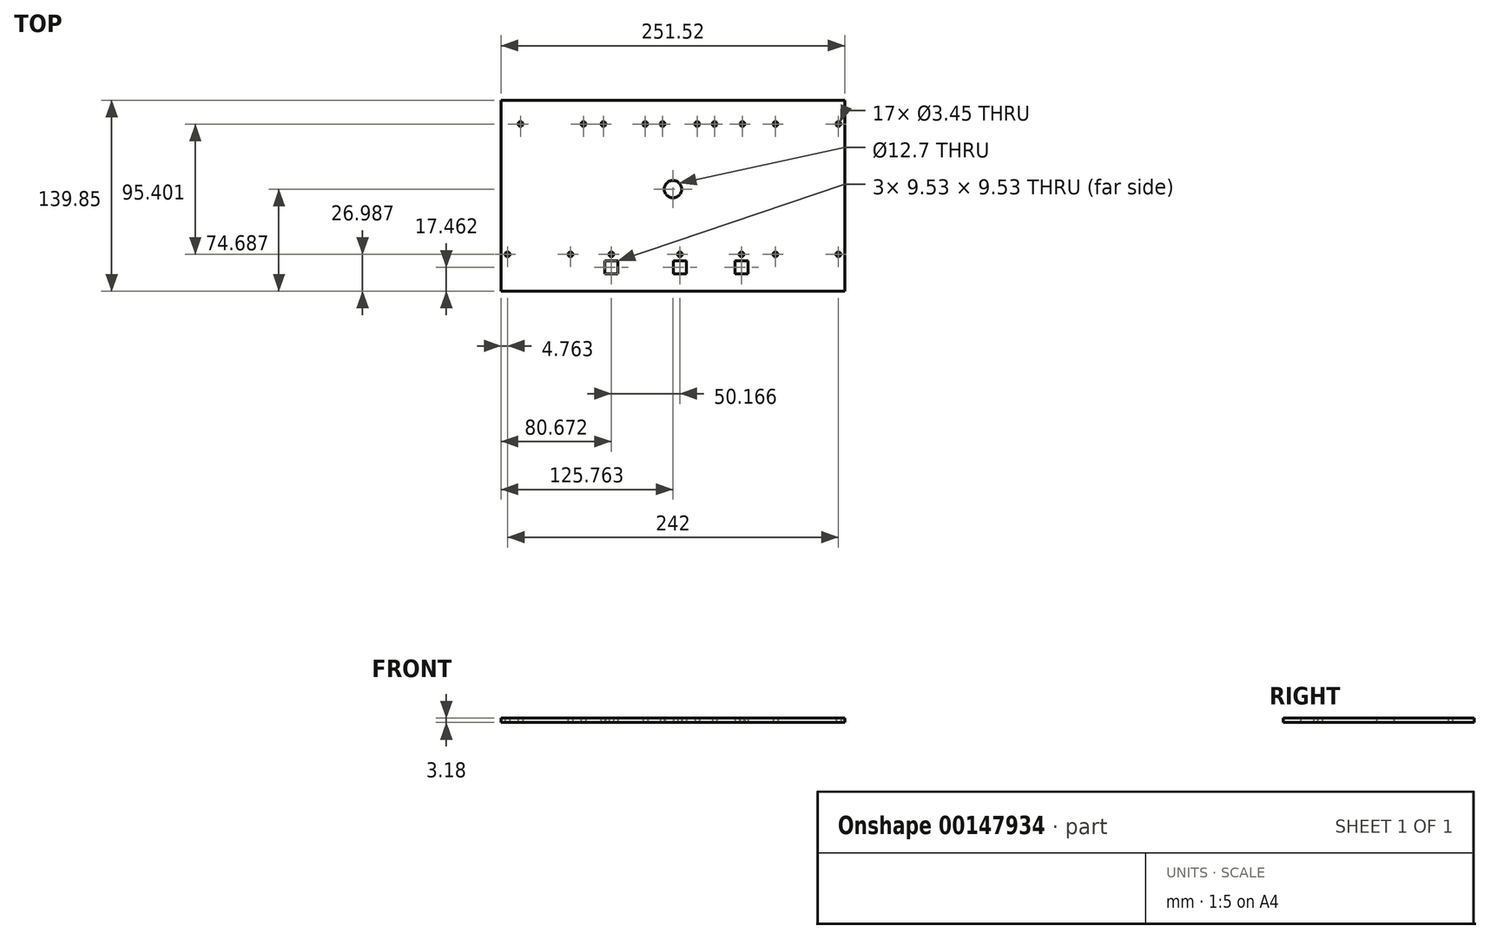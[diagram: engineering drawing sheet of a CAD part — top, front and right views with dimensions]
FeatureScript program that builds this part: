
annotation { "Feature Type Name" : "Feature", "Feature Type Description" : "" }
export const myFeature = defineFeature(function(context is Context, id is Id, definition is map)
    precondition{}
    {
        {
            var Q0;
            Q0=qCreatedBy(makeId("Top.planeOp"),FACE);
            var sketch = newSketch(context, id + "F0", { "sketchPlane" : qUnion([Q0])});
            skLineSegment(sketch, "E0.bottom", {"start": v(0, 0) * mm, "end": v(251.52, 0) * mm});
            skLineSegment(sketch, "E0.top", {"start": v(0, -139.85) * mm, "end": v(251.52, -139.85) * mm});
            skLineSegment(sketch, "E0.left", {"start": v(0, 0) * mm, "end": v(0, -139.85) * mm});
            skLineSegment(sketch, "E0.right", {"start": v(251.52, 0) * mm, "end": v(251.52, -139.85) * mm});
            skLineSegment(sketch, "E1", {"start": v(14.29, 0) * mm, "end": v(14.29, -17.46) * mm, "construction": true});
            skLineSegment(sketch, "E2", {"start": v(14.29, -17.46) * mm, "end": v(0, -17.46) * mm, "construction": true});
            skLineSegment(sketch, "E3", {"start": v(14.29, -17.46) * mm, "end": v(60.33, -17.46) * mm, "construction": true});
            skCircle(sketch, "E4", {"center": v(14.29, -17.46) * mm, "radius": 1.73 * mm});
            skCircle(sketch, "E5", {"center": v(60.33, -17.46) * mm, "radius": 1.73 * mm});
            skLineSegment(sketch, "E6", {"start": v(251.52, -17.46) * mm, "end": v(246.76, -17.46) * mm, "construction": true});
            skLineSegment(sketch, "E7", {"start": v(246.76, -17.46) * mm, "end": v(200.72, -17.46) * mm, "construction": true});
            skLineSegment(sketch, "E8", {"start": v(200.72, -17.46) * mm, "end": v(176.6, -17.46) * mm, "construction": true});
            skCircle(sketch, "E9", {"center": v(105.46, -17.46) * mm, "radius": 1.73 * mm});
            skCircle(sketch, "E10", {"center": v(176.6, -17.46) * mm, "radius": 1.73 * mm});
            skCircle(sketch, "E11", {"center": v(200.72, -17.46) * mm, "radius": 1.73 * mm});
            skCircle(sketch, "E12", {"center": v(246.76, -17.46) * mm, "radius": 1.73 * mm});
            skLineSegment(sketch, "E13", {"start": v(4.76, -139.85) * mm, "end": v(4.76, -112.86) * mm, "construction": true});
            skLineSegment(sketch, "E14", {"start": v(4.76, -112.86) * mm, "end": v(50.8, -112.86) * mm, "construction": true});
            skLineSegment(sketch, "E15", {"start": v(186.12, -112.86) * mm, "end": v(200.72, -112.86) * mm, "construction": true});
            skLineSegment(sketch, "E16", {"start": v(200.72, -112.86) * mm, "end": v(246.76, -112.86) * mm, "construction": true});
            skLineSegment(sketch, "E17", {"start": v(246.76, -112.86) * mm, "end": v(251.52, -112.86) * mm, "construction": true});
            skCircle(sketch, "E18", {"center": v(4.76, -112.86) * mm, "radius": 1.73 * mm});
            skCircle(sketch, "E19", {"center": v(50.8, -112.86) * mm, "radius": 1.73 * mm});
            skCircle(sketch, "E20", {"center": v(200.72, -112.86) * mm, "radius": 1.73 * mm});
            skCircle(sketch, "E21", {"center": v(246.76, -112.86) * mm, "radius": 1.73 * mm});
            skLineSegment(sketch, "E22", {"start": v(50.8, -112.86) * mm, "end": v(65.4, -112.86) * mm, "construction": true});
            skLineSegment(sketch, "E23", {"start": v(65.4, -112.86) * mm, "end": v(95.94, -112.86) * mm, "construction": true});
            skLineSegment(sketch, "E24", {"start": v(60.33, -17.46) * mm, "end": v(74.93, -17.46) * mm, "construction": true});
            skCircle(sketch, "E25", {"center": v(74.93, -17.46) * mm, "radius": 1.73 * mm});
            skLineSegment(sketch, "E26", {"start": v(74.93, -17.46) * mm, "end": v(105.46, -17.46) * mm, "construction": true});
            skLineSegment(sketch, "E27", {"start": v(186.12, -112.86) * mm, "end": v(165.74, -112.86) * mm, "construction": true});
            skLineSegment(sketch, "E28", {"start": v(176.6, -17.46) * mm, "end": v(156.21, -17.46) * mm, "construction": true});
            skCircle(sketch, "E29", {"center": v(156.21, -17.46) * mm, "radius": 1.73 * mm});
            skLineSegment(sketch, "E30", {"start": v(165.74, -112.86) * mm, "end": v(153.04, -112.86) * mm, "construction": true});
            skLineSegment(sketch, "E31", {"start": v(95.94, -112.86) * mm, "end": v(108.64, -112.86) * mm, "construction": true});
            skLineSegment(sketch, "E32", {"start": v(156.21, -17.46) * mm, "end": v(143.51, -17.46) * mm, "construction": true});
            skLineSegment(sketch, "E33", {"start": v(105.46, -17.46) * mm, "end": v(118.16, -17.46) * mm, "construction": true});
            skCircle(sketch, "E34", {"center": v(143.51, -17.46) * mm, "radius": 1.73 * mm});
            skCircle(sketch, "E35", {"center": v(118.16, -17.46) * mm, "radius": 1.73 * mm});
            skLineSegment(sketch, "E36", {"start": v(108.64, -112.86) * mm, "end": v(108.64, -65.16) * mm, "construction": true});
            skLineSegment(sketch, "E37", {"start": v(108.64, -65.16) * mm, "end": v(125.76, -65.16) * mm, "construction": true});
            skLineSegment(sketch, "E38", {"start": v(118.16, -17.46) * mm, "end": v(125.76, -17.46) * mm, "construction": true});
            skLineSegment(sketch, "E39", {"start": v(125.76, -65.16) * mm, "end": v(125.76, -17.46) * mm, "construction": true});
            skLineSegment(sketch, "E40", {"start": v(125.76, -17.46) * mm, "end": v(125.76, 0) * mm, "construction": true});
            skCircle(sketch, "E41", {"center": v(125.76, -65.16) * mm, "radius": 6.35 * mm});
            skLineSegment(sketch, "E42", {"start": v(4.76, -112.86) * mm, "end": v(0, -112.86) * mm, "construction": true});
            skCircle(sketch, "E43", {"center": v(80.67, -112.86) * mm, "radius": 1.73 * mm});
            skLineSegment(sketch, "E44.bottom", {"start": v(85.43, -127.15) * mm, "end": v(75.9, -127.15) * mm});
            skLineSegment(sketch, "E44.top", {"start": v(85.43, -117.63) * mm, "end": v(75.9, -117.63) * mm});
            skLineSegment(sketch, "E44.left", {"start": v(85.43, -127.15) * mm, "end": v(85.43, -117.63) * mm});
            skLineSegment(sketch, "E44.right", {"start": v(75.9, -127.15) * mm, "end": v(75.9, -117.63) * mm});
            skLineSegment(sketch, "E45", {"start": v(108.64, -112.86) * mm, "end": v(153.04, -112.86) * mm, "construction": true});
            skCircle(sketch, "E46", {"center": v(130.84, -112.86) * mm, "radius": 1.73 * mm});
            skCircle(sketch, "E47", {"center": v(175.93, -112.86) * mm, "radius": 1.73 * mm});
            skLineSegment(sketch, "E48.bottom", {"start": v(171.17, -117.63) * mm, "end": v(180.7, -117.63) * mm});
            skLineSegment(sketch, "E48.top", {"start": v(171.17, -127.15) * mm, "end": v(180.7, -127.15) * mm});
            skLineSegment(sketch, "E48.left", {"start": v(171.17, -117.63) * mm, "end": v(171.17, -127.15) * mm});
            skLineSegment(sketch, "E48.right", {"start": v(180.7, -117.63) * mm, "end": v(180.7, -127.15) * mm});
            skLineSegment(sketch, "E49.bottom", {"start": v(126.08, -117.63) * mm, "end": v(135.6, -117.63) * mm});
            skLineSegment(sketch, "E49.top", {"start": v(126.08, -127.15) * mm, "end": v(135.6, -127.15) * mm});
            skLineSegment(sketch, "E49.left", {"start": v(126.08, -117.63) * mm, "end": v(126.08, -127.15) * mm});
            skLineSegment(sketch, "E49.right", {"start": v(135.6, -117.63) * mm, "end": v(135.6, -127.15) * mm});
            skLineSegment(sketch, "E50", {"start": v(80.67, -112.86) * mm, "end": v(80.67, -117.63) * mm, "construction": true});
            skLineSegment(sketch, "E51", {"start": v(130.84, -112.86) * mm, "end": v(130.84, -117.63) * mm, "construction": true});
            skLineSegment(sketch, "E52", {"start": v(175.93, -112.86) * mm, "end": v(175.93, -117.63) * mm, "construction": true});
            skSolve(sketch);
        }
        {
            var Q0;
            Q0=qSketchRegion(id+"F0",true);
            extrude(context, id + "F1", {"entities" : qUnion([Q0]), "depth" : 3.17 * mm});
        }
    });
